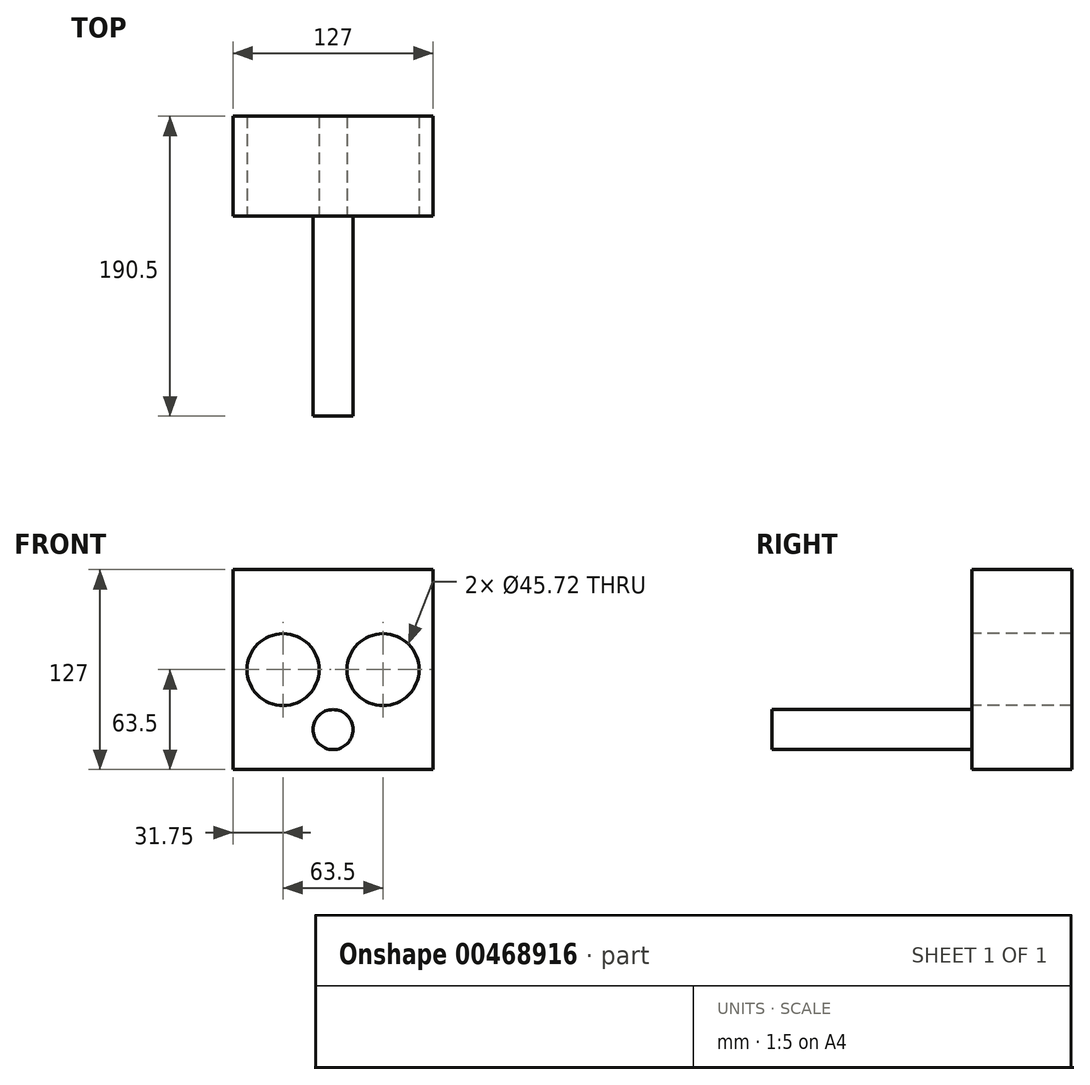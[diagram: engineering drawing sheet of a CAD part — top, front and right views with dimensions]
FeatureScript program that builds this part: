
annotation { "Feature Type Name" : "Feature", "Feature Type Description" : "" }
export const myFeature = defineFeature(function(context is Context, id is Id, definition is map)
    precondition{}
    {
        {
            var Q0;
            Q0=qCreatedBy(makeId("Front.planeOp"),FACE);
            var sketch = newSketch(context, id + "F0", { "sketchPlane" : qUnion([Q0])});
            skLineSegment(sketch, "E0.bottom", {"start": v(63.5, -63.5) * mm, "end": v(-63.5, -63.5) * mm});
            skLineSegment(sketch, "E0.top", {"start": v(63.5, 63.5) * mm, "end": v(-63.5, 63.5) * mm});
            skLineSegment(sketch, "E0.left", {"start": v(63.5, -63.5) * mm, "end": v(63.5, 63.5) * mm});
            skLineSegment(sketch, "E0.right", {"start": v(-63.5, -63.5) * mm, "end": v(-63.5, 63.5) * mm});
            skPoint(sketch, "E0.middle", {"position": v(0, 0) * mm});
            skCircle(sketch, "E1", {"center": v(-31.75, 0) * mm, "radius": 22.86 * mm});
            skCircle(sketch, "E2", {"center": v(31.75, 0) * mm, "radius": 22.86 * mm});
            skSolve(sketch);
        }
        {
            var Q0;
            Q0=makeQuery(id+"F0.imprint","IMPRINT",FACE,{"disambiguationData":[TD([[makeQuery(id+"F0.imprint","IMPRINT",EDGE,{"derivedFrom":sQuery(id+"F0.wireOp",EDGE,"E0.bottom")}),-1.0]])]});
            extrude(context, id + "F1", {"entities" : qUnion([Q0]), "oppositeDirection" : true, "depth" : 63.5 * mm});
        }
        {
            var Q0;
            Q0=makeQuery(id+"F1.opExtrude","CAP_FACE",FACE,{"disambiguationData":[OSD([sQuery(id+"F0.wireOp",EDGE,"E0.bottom"),sQuery(id+"F0.wireOp",EDGE,"E0.top"),sQuery(id+"F0.wireOp",EDGE,"E0.left"),sQuery(id+"F0.wireOp",EDGE,"E0.right"),sQuery(id+"F0.wireOp",EDGE,"E1"),sQuery(id+"F0.wireOp",EDGE,"E2")])],"isStart":true});
            var sketch = newSketch(context, id + "F2", { "sketchPlane" : qUnion([Q0])});
            skCircle(sketch, "E3", {"center": v(0, -38.1) * mm, "radius": 12.7 * mm});
            skSolve(sketch);
        }
        {
            var Q0;
            Q0=qSketchRegion(id+"F2",true);
            extrude(context, id + "F3", {"entities" : qUnion([Q0]), "operationType" : NewBodyOperationType.ADD, "depth" : 127 * mm});
        }
    });
